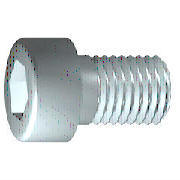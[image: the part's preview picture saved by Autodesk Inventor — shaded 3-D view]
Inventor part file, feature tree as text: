
AUTODESK INVENTOR PART (.ipt)
format: ipt  version: 2019 (Build 230136000, 136)  size: 196,096 bytes
history: native  units: mm (DEFAULTED — no unit token found)
features: sketch x2, other x1, extrude x1, plane x1, fillet x1
ambient origin geometry x7: Origin, YZ Plane, XY Plane, X Axis, Y Axis, Z Axis, Center Point
bodies: Solid1 (feature_tree)
feature tree (6):
  other  "Körper"
  extrude  "Loch"  Depth=3.0mm
  plane  "Work Plane1"
  fillet  "Fillet2"  Radius=3.0mm
  sketch  "Skizze1"  dims[d1=6.75mm d2=0.306825mm d3=3.0mm]
  sketch  "Skizze2"  dims[d4=1.3mm d5=60.0deg d6=3.0mm d7=3.0mm d8=2.886751mm d9=5.5mm d10=90.0deg d11=10.0mm d12=0.0mm d13=6.75mm d14=0.0mm d15=0.306725mm d16=0.306725mm d17=0.3mm d19=0.0mm d26=8.0mm d27=45.0deg d28=0.0mm d29=0.0mm d30=0.1mm]
